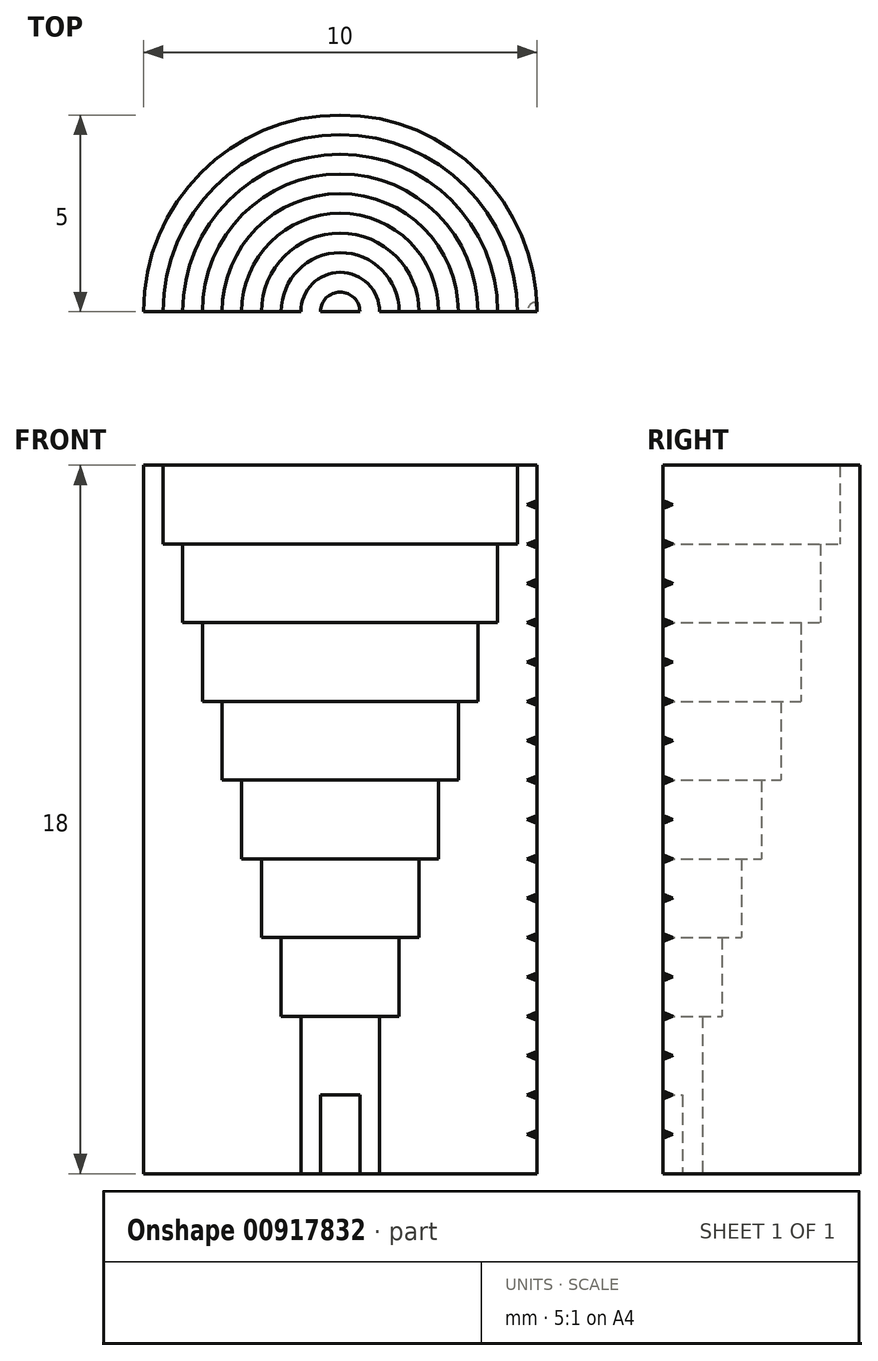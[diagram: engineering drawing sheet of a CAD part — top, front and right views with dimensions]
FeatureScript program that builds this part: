
annotation { "Feature Type Name" : "Feature", "Feature Type Description" : "" }
export const myFeature = defineFeature(function(context is Context, id is Id, definition is map)
    precondition{}
    {
        {
            var Q0;
            Q0=qCreatedBy(makeId("Top.planeOp"),FACE);
            var sketch = newSketch(context, id + "F0", { "sketchPlane" : qUnion([Q0])});
            skArc(sketch, "E0", {"start": v(-0.5, 0) * mm, "mid": v(0, 0.5) * mm, "end": v(0.5, 0) * mm});
            skLineSegment(sketch, "E1", {"start": v(0, 0) * mm, "end": v(0.5, 0) * mm});
            skLineSegment(sketch, "E2", {"start": v(1, 0) * mm, "end": v(1.5, 0) * mm});
            skLineSegment(sketch, "E3", {"start": v(1.5, 0) * mm, "end": v(2, 0) * mm});
            skLineSegment(sketch, "E4", {"start": v(2, 0) * mm, "end": v(2.5, 0) * mm});
            skLineSegment(sketch, "E5", {"start": v(0.5, 0) * mm, "end": v(1, 0) * mm});
            skLineSegment(sketch, "E6", {"start": v(2.5, 0) * mm, "end": v(3, 0) * mm});
            skLineSegment(sketch, "E7", {"start": v(3, 0) * mm, "end": v(3.5, 0) * mm});
            skLineSegment(sketch, "E8", {"start": v(3.5, 0) * mm, "end": v(4, 0) * mm});
            skLineSegment(sketch, "E9", {"start": v(4, 0) * mm, "end": v(4.5, 0) * mm});
            skLineSegment(sketch, "E10", {"start": v(4.5, 0) * mm, "end": v(5, 0) * mm});
            skArc(sketch, "E11", {"start": v(5, 0) * mm, "mid": v(0, 5) * mm, "end": v(-5, 0) * mm});
            skLineSegment(sketch, "E12", {"start": v(-5, 0) * mm, "end": v(0, 0) * mm});
            skArc(sketch, "E13", {"start": v(1, 0) * mm, "mid": v(0, 1) * mm, "end": v(-1, 0) * mm});
            skArc(sketch, "E14", {"start": v(1.5, 0) * mm, "mid": v(0, 1.5) * mm, "end": v(-1.5, 0) * mm});
            skArc(sketch, "E15", {"start": v(2, 0) * mm, "mid": v(0, 2) * mm, "end": v(-2, 0) * mm});
            skArc(sketch, "E16", {"start": v(2.5, 0) * mm, "mid": v(0, 2.5) * mm, "end": v(-2.5, 0) * mm});
            skArc(sketch, "E17", {"start": v(3, 0) * mm, "mid": v(0, 3) * mm, "end": v(-3, 0) * mm});
            skArc(sketch, "E18", {"start": v(3.5, 0) * mm, "mid": v(0, 3.5) * mm, "end": v(-3.5, 0) * mm});
            skArc(sketch, "E19", {"start": v(4, 0) * mm, "mid": v(0, 4) * mm, "end": v(-4, 0) * mm});
            skArc(sketch, "E20", {"start": v(4.5, 0) * mm, "mid": v(0, 4.5) * mm, "end": v(-4.5, 0) * mm});
            skSolve(sketch);
        }
        {
            var Q0;
            Q0=makeQuery(id+"F0.imprint","IMPRINT",FACE,{"disambiguationData":[TD([[makeQuery(id+"F0.imprint","IMPRINT",EDGE,{"derivedFrom":sQuery(id+"F0.wireOp",EDGE,"E10")}),1.0]])]});
            extrude(context, id + "F1", {"entities" : qUnion([Q0]), "depth" : 18 * mm, "offsetDistance" : 25 * mm});
        }
        {
            var Q0;
            Q0=makeQuery(id+"F0.imprint","IMPRINT",FACE,{"disambiguationData":[TD([[makeQuery(id+"F0.imprint","IMPRINT",EDGE,{"derivedFrom":sQuery(id+"F0.wireOp",EDGE,"E9")}),1.0]])]});
            extrude(context, id + "F2", {"entities" : qUnion([Q0]), "operationType" : NewBodyOperationType.ADD, "depth" : 16 * mm, "offsetDistance" : 25 * mm});
        }
        {
            var Q0;
            Q0=makeQuery(id+"F0.imprint","IMPRINT",FACE,{"disambiguationData":[TD([[makeQuery(id+"F0.imprint","IMPRINT",EDGE,{"derivedFrom":sQuery(id+"F0.wireOp",EDGE,"E8")}),1.0]])]});
            extrude(context, id + "F3", {"entities" : qUnion([Q0]), "operationType" : NewBodyOperationType.ADD, "depth" : 14 * mm, "offsetDistance" : 25 * mm});
        }
        {
            var Q0;
            Q0=makeQuery(id+"F0.imprint","IMPRINT",FACE,{"disambiguationData":[TD([[makeQuery(id+"F0.imprint","IMPRINT",EDGE,{"derivedFrom":sQuery(id+"F0.wireOp",EDGE,"E7")}),1.0]])]});
            extrude(context, id + "F4", {"entities" : qUnion([Q0]), "operationType" : NewBodyOperationType.ADD, "depth" : 12 * mm, "offsetDistance" : 25 * mm});
        }
        {
            var Q0;
            Q0=makeQuery(id+"F0.imprint","IMPRINT",FACE,{"disambiguationData":[TD([[makeQuery(id+"F0.imprint","IMPRINT",EDGE,{"derivedFrom":sQuery(id+"F0.wireOp",EDGE,"E6")}),1.0]])]});
            extrude(context, id + "F5", {"entities" : qUnion([Q0]), "operationType" : NewBodyOperationType.ADD, "depth" : 10 * mm, "offsetDistance" : 25 * mm});
        }
        {
            var Q0;
            Q0=makeQuery(id+"F0.imprint","IMPRINT",FACE,{"disambiguationData":[TD([[makeQuery(id+"F0.imprint","IMPRINT",EDGE,{"derivedFrom":sQuery(id+"F0.wireOp",EDGE,"E4")}),1.0]])]});
            extrude(context, id + "F6", {"entities" : qUnion([Q0]), "operationType" : NewBodyOperationType.ADD, "depth" : 8 * mm, "offsetDistance" : 25 * mm});
        }
        {
            var Q0;
            Q0=makeQuery(id+"F0.imprint","IMPRINT",FACE,{"disambiguationData":[TD([[makeQuery(id+"F0.imprint","IMPRINT",EDGE,{"derivedFrom":sQuery(id+"F0.wireOp",EDGE,"E3")}),1.0]])]});
            extrude(context, id + "F7", {"entities" : qUnion([Q0]), "operationType" : NewBodyOperationType.ADD, "depth" : 6 * mm, "offsetDistance" : 25 * mm});
        }
        {
            var Q0;
            Q0=makeQuery(id+"F0.imprint","IMPRINT",FACE,{"disambiguationData":[TD([[makeQuery(id+"F0.imprint","IMPRINT",EDGE,{"derivedFrom":sQuery(id+"F0.wireOp",EDGE,"E2")}),1.0]])]});
            extrude(context, id + "F8", {"entities" : qUnion([Q0]), "operationType" : NewBodyOperationType.ADD, "depth" : 4 * mm, "offsetDistance" : 25 * mm});
        }
        {
            var Q0;
            {var subQ0=sQuery(id+"F0.wireOp",EDGE,"E0");Q0=makeQuery(id+"F0.imprint","IMPRINT",FACE,{"disambiguationData":[TD([[makeQuery(id+"F0.imprint","IMPRINT",EDGE,{"derivedFrom":subQ0}),1.0]])]});}
            extrude(context, id + "F9", {"entities" : qUnion([Q0]), "operationType" : NewBodyOperationType.ADD, "depth" : 2 * mm, "offsetDistance" : 25 * mm});
        }
        {
            var Q0;
            Q0=qCreatedBy(makeId("Front.planeOp"),FACE);
            var sketch = newSketch(context, id + "F10", { "sketchPlane" : qUnion([Q0])});
            skLineSegment(sketch, "E21", {"start": v(-5, 2) * mm, "end": v(5, 2) * mm, "construction": true});
            skLineSegment(sketch, "E22", {"start": v(-5, 4) * mm, "end": v(5, 4) * mm, "construction": true});
            skLineSegment(sketch, "E23", {"start": v(-5, 6) * mm, "end": v(5, 6) * mm, "construction": true});
            skLineSegment(sketch, "E24", {"start": v(-5, 8) * mm, "end": v(5, 8) * mm, "construction": true});
            skLineSegment(sketch, "E25", {"start": v(-5, 10) * mm, "end": v(5, 10) * mm, "construction": true});
            skLineSegment(sketch, "E26", {"start": v(-5, 12) * mm, "end": v(5, 12) * mm, "construction": true});
            skLineSegment(sketch, "E27", {"start": v(-5, 14) * mm, "end": v(5, 14) * mm, "construction": true});
            skLineSegment(sketch, "E28", {"start": v(-5, 16) * mm, "end": v(5, 16) * mm, "construction": true});
            skLineSegment(sketch, "E29", {"start": v(4.75, 18) * mm, "end": v(4.75, 16) * mm, "construction": true});
            skLineSegment(sketch, "E30", {"start": v(4.75, 17) * mm, "end": v(5, 17.1) * mm});
            skLineSegment(sketch, "E31", {"start": v(5, 17.1) * mm, "end": v(5, 16.9) * mm});
            skLineSegment(sketch, "E32", {"start": v(5, 16.9) * mm, "end": v(4.75, 17) * mm});
            skLineSegment(sketch, "E33.1.0.0", {"start": v(5, 15.9) * mm, "end": v(4.75, 16) * mm});
            skLineSegment(sketch, "E33.1.0.1", {"start": v(4.75, 16) * mm, "end": v(5, 16.1) * mm});
            skLineSegment(sketch, "E33.1.0.2", {"start": v(5, 16.1) * mm, "end": v(5, 15.9) * mm});
            skLineSegment(sketch, "E33.2.0.0", {"start": v(5, 14.9) * mm, "end": v(4.75, 15) * mm});
            skLineSegment(sketch, "E33.2.0.1", {"start": v(4.75, 15) * mm, "end": v(5, 15.1) * mm});
            skLineSegment(sketch, "E33.2.0.2", {"start": v(5, 15.1) * mm, "end": v(5, 14.9) * mm});
            skLineSegment(sketch, "E33.3.0.0", {"start": v(5, 13.9) * mm, "end": v(4.75, 14) * mm});
            skLineSegment(sketch, "E33.3.0.1", {"start": v(4.75, 14) * mm, "end": v(5, 14.1) * mm});
            skLineSegment(sketch, "E33.3.0.2", {"start": v(5, 14.1) * mm, "end": v(5, 13.9) * mm});
            skLineSegment(sketch, "E33.4.0.0", {"start": v(5, 12.9) * mm, "end": v(4.75, 13) * mm});
            skLineSegment(sketch, "E33.4.0.1", {"start": v(4.75, 13) * mm, "end": v(5, 13.1) * mm});
            skLineSegment(sketch, "E33.4.0.2", {"start": v(5, 13.1) * mm, "end": v(5, 12.9) * mm});
            skLineSegment(sketch, "E33.5.0.0", {"start": v(5, 11.9) * mm, "end": v(4.75, 12) * mm});
            skLineSegment(sketch, "E33.5.0.1", {"start": v(4.75, 12) * mm, "end": v(5, 12.1) * mm});
            skLineSegment(sketch, "E33.5.0.2", {"start": v(5, 12.1) * mm, "end": v(5, 11.9) * mm});
            skLineSegment(sketch, "E33.6.0.0", {"start": v(5, 10.9) * mm, "end": v(4.75, 11) * mm});
            skLineSegment(sketch, "E33.6.0.1", {"start": v(4.75, 11) * mm, "end": v(5, 11.1) * mm});
            skLineSegment(sketch, "E33.6.0.2", {"start": v(5, 11.1) * mm, "end": v(5, 10.9) * mm});
            skLineSegment(sketch, "E33.7.0.0", {"start": v(5, 9.9) * mm, "end": v(4.75, 10) * mm});
            skLineSegment(sketch, "E33.7.0.1", {"start": v(4.75, 10) * mm, "end": v(5, 10.1) * mm});
            skLineSegment(sketch, "E33.7.0.2", {"start": v(5, 10.1) * mm, "end": v(5, 9.9) * mm});
            skLineSegment(sketch, "E33.8.0.0", {"start": v(5, 8.9) * mm, "end": v(4.75, 9) * mm});
            skLineSegment(sketch, "E33.8.0.1", {"start": v(4.75, 9) * mm, "end": v(5, 9.1) * mm});
            skLineSegment(sketch, "E33.8.0.2", {"start": v(5, 9.1) * mm, "end": v(5, 8.9) * mm});
            skLineSegment(sketch, "E33.9.0.0", {"start": v(5, 7.9) * mm, "end": v(4.75, 8) * mm});
            skLineSegment(sketch, "E33.9.0.1", {"start": v(4.75, 8) * mm, "end": v(5, 8.1) * mm});
            skLineSegment(sketch, "E33.9.0.2", {"start": v(5, 8.1) * mm, "end": v(5, 7.9) * mm});
            skLineSegment(sketch, "E33.10.0.0", {"start": v(5, 6.9) * mm, "end": v(4.75, 7) * mm});
            skLineSegment(sketch, "E33.10.0.1", {"start": v(4.75, 7) * mm, "end": v(5, 7.1) * mm});
            skLineSegment(sketch, "E33.10.0.2", {"start": v(5, 7.1) * mm, "end": v(5, 6.9) * mm});
            skLineSegment(sketch, "E33.11.0.0", {"start": v(5, 5.9) * mm, "end": v(4.75, 6) * mm});
            skLineSegment(sketch, "E33.11.0.1", {"start": v(4.75, 6) * mm, "end": v(5, 6.1) * mm});
            skLineSegment(sketch, "E33.11.0.2", {"start": v(5, 6.1) * mm, "end": v(5, 5.9) * mm});
            skLineSegment(sketch, "E33.12.0.0", {"start": v(5, 4.9) * mm, "end": v(4.75, 5) * mm});
            skLineSegment(sketch, "E33.12.0.1", {"start": v(4.75, 5) * mm, "end": v(5, 5.1) * mm});
            skLineSegment(sketch, "E33.12.0.2", {"start": v(5, 5.1) * mm, "end": v(5, 4.9) * mm});
            skLineSegment(sketch, "E33.13.0.0", {"start": v(5, 3.9) * mm, "end": v(4.75, 4) * mm});
            skLineSegment(sketch, "E33.13.0.1", {"start": v(4.75, 4) * mm, "end": v(5, 4.1) * mm});
            skLineSegment(sketch, "E33.13.0.2", {"start": v(5, 4.1) * mm, "end": v(5, 3.9) * mm});
            skLineSegment(sketch, "E33.14.0.0", {"start": v(5, 2.9) * mm, "end": v(4.75, 3) * mm});
            skLineSegment(sketch, "E33.14.0.1", {"start": v(4.75, 3) * mm, "end": v(5, 3.1) * mm});
            skLineSegment(sketch, "E33.14.0.2", {"start": v(5, 3.1) * mm, "end": v(5, 2.9) * mm});
            skLineSegment(sketch, "E33.15.0.0", {"start": v(5, 1.9) * mm, "end": v(4.75, 2) * mm});
            skLineSegment(sketch, "E33.15.0.1", {"start": v(4.75, 2) * mm, "end": v(5, 2.1) * mm});
            skLineSegment(sketch, "E33.15.0.2", {"start": v(5, 2.1) * mm, "end": v(5, 1.9) * mm});
            skLineSegment(sketch, "E33.16.0.0", {"start": v(5, 0.9) * mm, "end": v(4.75, 1) * mm});
            skLineSegment(sketch, "E33.16.0.1", {"start": v(4.75, 1) * mm, "end": v(5, 1.1) * mm});
            skLineSegment(sketch, "E33.16.0.2", {"start": v(5, 1.1) * mm, "end": v(5, 0.9) * mm});
            skLineSegment(sketch, "E33.direction1", {"start": v(4.75, 17) * mm, "end": v(4.75, 16) * mm, "construction": true});
            skSolve(sketch);
        }
        {
            var Q0;
            Q0=makeQuery(id+"F10.imprint","IMPRINT",FACE,{"disambiguationData":[TD([[makeQuery(id+"F10.imprint","IMPRINT",EDGE,{"derivedFrom":sQuery(id+"F10.wireOp",EDGE,"E30")}),-1.0]])]});
            var Q1;
            Q1=makeQuery(id+"F10.imprint","IMPRINT",FACE,{"disambiguationData":[TD([[makeQuery(id+"F10.imprint","IMPRINT",EDGE,{"derivedFrom":sQuery(id+"F10.wireOp",EDGE,"E33.1.0.0")}),-1.0]])]});
            var Q2;
            Q2=makeQuery(id+"F10.imprint","IMPRINT",FACE,{"disambiguationData":[TD([[makeQuery(id+"F10.imprint","IMPRINT",EDGE,{"derivedFrom":sQuery(id+"F10.wireOp",EDGE,"E33.2.0.0")}),-1.0]])]});
            var Q3;
            Q3=makeQuery(id+"F10.imprint","IMPRINT",FACE,{"disambiguationData":[TD([[makeQuery(id+"F10.imprint","IMPRINT",EDGE,{"derivedFrom":sQuery(id+"F10.wireOp",EDGE,"E33.3.0.0")}),-1.0]])]});
            var Q4;
            Q4=makeQuery(id+"F10.imprint","IMPRINT",FACE,{"disambiguationData":[TD([[makeQuery(id+"F10.imprint","IMPRINT",EDGE,{"derivedFrom":sQuery(id+"F10.wireOp",EDGE,"E33.4.0.0")}),-1.0]])]});
            var Q5;
            Q5=makeQuery(id+"F10.imprint","IMPRINT",FACE,{"disambiguationData":[TD([[makeQuery(id+"F10.imprint","IMPRINT",EDGE,{"derivedFrom":sQuery(id+"F10.wireOp",EDGE,"E33.5.0.0")}),-1.0]])]});
            var Q6;
            Q6=makeQuery(id+"F10.imprint","IMPRINT",FACE,{"disambiguationData":[TD([[makeQuery(id+"F10.imprint","IMPRINT",EDGE,{"derivedFrom":sQuery(id+"F10.wireOp",EDGE,"E33.6.0.0")}),-1.0]])]});
            var Q7;
            Q7=makeQuery(id+"F10.imprint","IMPRINT",FACE,{"disambiguationData":[TD([[makeQuery(id+"F10.imprint","IMPRINT",EDGE,{"derivedFrom":sQuery(id+"F10.wireOp",EDGE,"E33.7.0.0")}),-1.0]])]});
            var Q8;
            Q8=makeQuery(id+"F10.imprint","IMPRINT",FACE,{"disambiguationData":[TD([[makeQuery(id+"F10.imprint","IMPRINT",EDGE,{"derivedFrom":sQuery(id+"F10.wireOp",EDGE,"E33.8.0.0")}),-1.0]])]});
            var Q9;
            Q9=makeQuery(id+"F10.imprint","IMPRINT",FACE,{"disambiguationData":[TD([[makeQuery(id+"F10.imprint","IMPRINT",EDGE,{"derivedFrom":sQuery(id+"F10.wireOp",EDGE,"E33.9.0.0")}),-1.0]])]});
            var Q10;
            Q10=makeQuery(id+"F10.imprint","IMPRINT",FACE,{"disambiguationData":[TD([[makeQuery(id+"F10.imprint","IMPRINT",EDGE,{"derivedFrom":sQuery(id+"F10.wireOp",EDGE,"E33.10.0.0")}),-1.0]])]});
            var Q11;
            Q11=makeQuery(id+"F10.imprint","IMPRINT",FACE,{"disambiguationData":[TD([[makeQuery(id+"F10.imprint","IMPRINT",EDGE,{"derivedFrom":sQuery(id+"F10.wireOp",EDGE,"E33.16.0.0")}),-1.0]])]});
            var Q12;
            Q12=makeQuery(id+"F10.imprint","IMPRINT",FACE,{"disambiguationData":[TD([[makeQuery(id+"F10.imprint","IMPRINT",EDGE,{"derivedFrom":sQuery(id+"F10.wireOp",EDGE,"E33.15.0.0")}),-1.0]])]});
            var Q13;
            Q13=makeQuery(id+"F10.imprint","IMPRINT",FACE,{"disambiguationData":[TD([[makeQuery(id+"F10.imprint","IMPRINT",EDGE,{"derivedFrom":sQuery(id+"F10.wireOp",EDGE,"E33.14.0.0")}),-1.0]])]});
            var Q14;
            Q14=makeQuery(id+"F10.imprint","IMPRINT",FACE,{"disambiguationData":[TD([[makeQuery(id+"F10.imprint","IMPRINT",EDGE,{"derivedFrom":sQuery(id+"F10.wireOp",EDGE,"E33.13.0.0")}),-1.0]])]});
            var Q15;
            Q15=makeQuery(id+"F10.imprint","IMPRINT",FACE,{"disambiguationData":[TD([[makeQuery(id+"F10.imprint","IMPRINT",EDGE,{"derivedFrom":sQuery(id+"F10.wireOp",EDGE,"E33.12.0.0")}),-1.0]])]});
            var Q16;
            Q16=makeQuery(id+"F10.imprint","IMPRINT",FACE,{"disambiguationData":[TD([[makeQuery(id+"F10.imprint","IMPRINT",EDGE,{"derivedFrom":sQuery(id+"F10.wireOp",EDGE,"E33.11.0.0")}),-1.0]])]});
            var Q17;
            Q17=makeQuery(id+"F1.opExtrude","SWEPT_EDGE",EDGE,{"disambiguationData":[OSD([sQuery(id+"F0.wireOp",EDGE,"E10"),sQuery(id+"F0.wireOp",EDGE,"E11")])]});
            revolve(context, id + "F11", {"operationType" : NewBodyOperationType.REMOVE, "surfaceOperationType" : NewSurfaceOperationType.NEW, "entities" : qUnion([Q0, Q1, Q2, Q3, Q4, Q5, Q6, Q7, Q8, Q9, Q10, Q11, Q12, Q13, Q14, Q15, Q16]), "axis" : qUnion([Q17]), "revolveType" : RevolveType.FULL, "oppositeDirection" : true});
        }
    });
